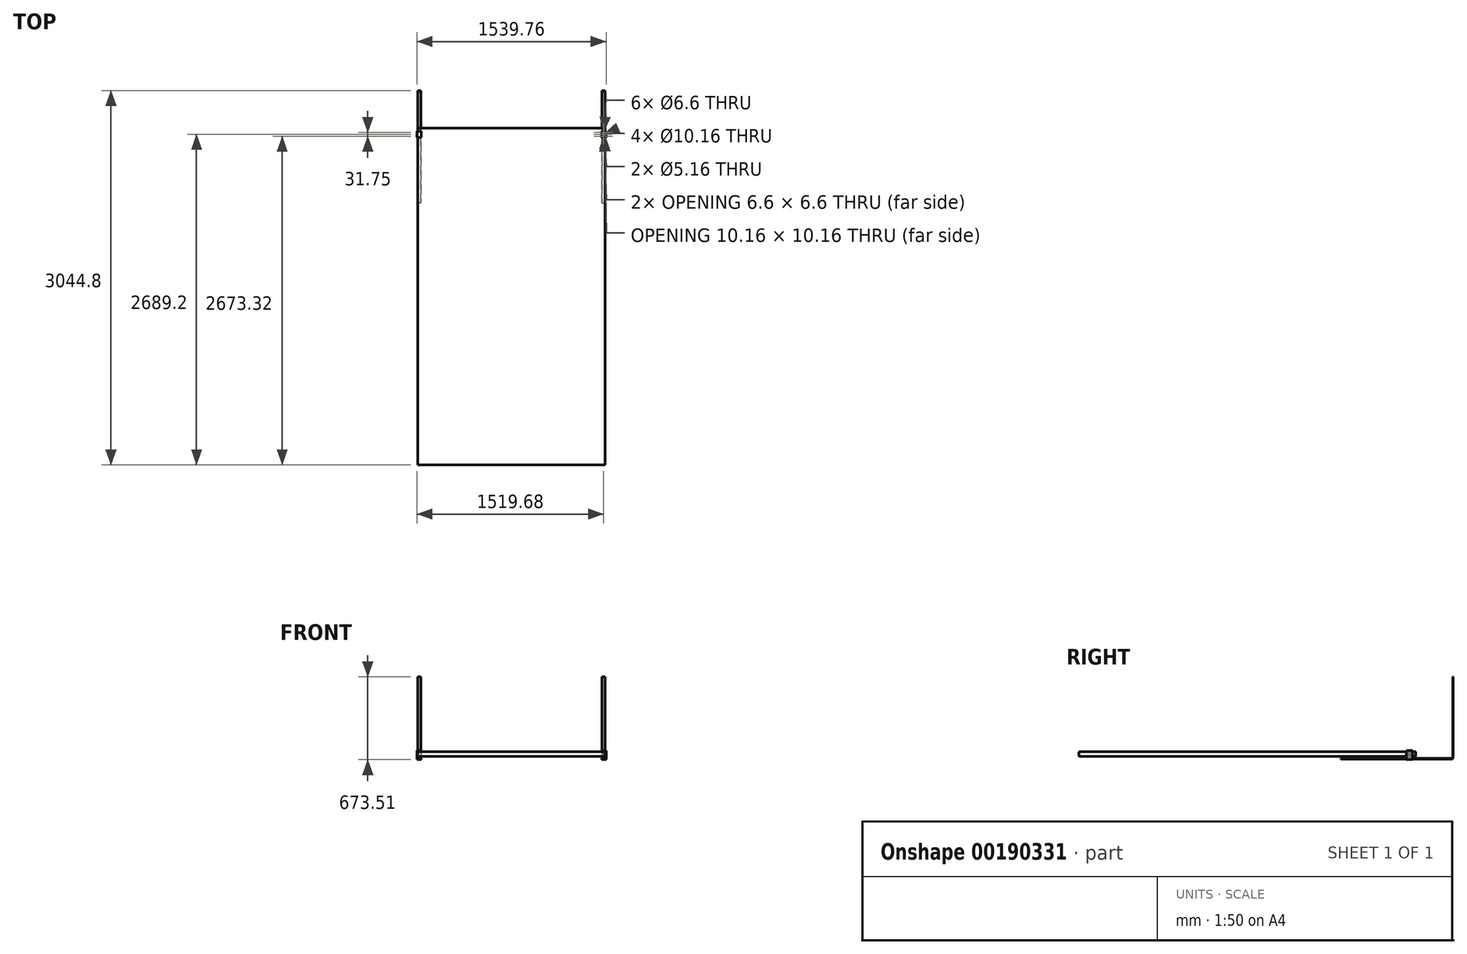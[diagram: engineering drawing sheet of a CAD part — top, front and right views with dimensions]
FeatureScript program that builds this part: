
annotation { "Feature Type Name" : "Feature", "Feature Type Description" : "" }
export const myFeature = defineFeature(function(context is Context, id is Id, definition is map)
    precondition{}
    {
        {
            var Q0;
            Q0=qCreatedBy(makeId("Top.planeOp"),FACE);
            var sketch = newSketch(context, id + "F0", { "sketchPlane" : qUnion([Q0])});
            skLineSegment(sketch, "E0.bottom", {"start": v(762.5, 1370) * mm, "end": v(-762.5, 1370) * mm});
            skLineSegment(sketch, "E0.top", {"start": v(762.5, -1370) * mm, "end": v(-762.5, -1370) * mm});
            skLineSegment(sketch, "E0.left", {"start": v(762.5, 1370) * mm, "end": v(762.5, -1370) * mm});
            skLineSegment(sketch, "E0.right", {"start": v(-762.5, 1370) * mm, "end": v(-762.5, -1370) * mm});
            skPoint(sketch, "E0.middle", {"position": v(0, 0) * mm});
            skSolve(sketch);
        }
        {
            var Q0;
            Q0 = qSketchRegion(id + "F0", true);
            extrude(context, id + "F1", {"entities" : qUnion([Q0]), "oppositeDirection" : true, "depth" : 38.1 * mm});
        }
        {
            var Q0;
            Q0=makeQuery(id+"F1.opExtrude","SWEPT_FACE",FACE,{"disambiguationData":[OSD([sQuery(id+"F0.wireOp",EDGE,"E0.bottom")])]});
            cPlane(context, id + "F2", {"entities" : qUnion([Q0]), "cplaneType" : CPlaneType.OFFSET, "offset" : 304.8 * mm, "width" : 152.4 * mm, "height" : 152.4 * mm});
        }
        {
            var Q0;
            Q0=makeQuery(id+"F1.opExtrude","SWEPT_FACE",FACE,{"disambiguationData":[OSD([sQuery(id+"F0.wireOp",EDGE,"E0.left")])]});
            cPlane(context, id + "F3", {"entities" : qUnion([Q0]), "cplaneType" : CPlaneType.OFFSET, "offset" : 0 * mm, "width" : 152.4 * mm, "height" : 152.4 * mm});
        }
        {
            var Q0;
            Q0=qCreatedBy(id+"F3.planeOp",FACE);
            var sketch = newSketch(context, id + "F4", { "sketchPlane" : qUnion([Q0])});
            skLineSegment(sketch, "E1", {"start": v(760.4, -54.06) * mm, "end": v(760.4, -58.83) * mm});
            skLineSegment(sketch, "E2", {"start": v(760.4, -58.83) * mm, "end": v(1663.69, -58.83) * mm});
            skLineSegment(sketch, "E3", {"start": v(1674.8, -47.71) * mm, "end": v(1674.8, 609.6) * mm});
            skLineSegment(sketch, "E4", {"start": v(1670.04, 609.6) * mm, "end": v(1674.8, 609.6) * mm});
            skLineSegment(sketch, "E5", {"start": v(1670.04, 609.6) * mm, "end": v(1670.04, -47.71) * mm});
            skLineSegment(sketch, "E6", {"start": v(1663.69, -54.06) * mm, "end": v(760.4, -54.06) * mm});
            skPoint(sketch, "E7.visualSharp", {"position": v(1670.04, -54.06) * mm});
            skArc(sketch, "E7.filletArc", {"start": v(1663.69, -54.06) * mm, "mid": v(1668.18, -52.2) * mm, "end": v(1670.04, -47.71) * mm});
            skPoint(sketch, "E8.visualSharp", {"position": v(1674.8, -58.83) * mm});
            skArc(sketch, "E8.filletArc", {"start": v(1663.69, -58.83) * mm, "mid": v(1671.55, -55.57) * mm, "end": v(1674.8, -47.71) * mm});
            skSolve(sketch);
        }
        {
            var Q0;
            Q0 = qSketchRegion(id + "F4", true);
            extrude(context, id + "F5", {"entities" : qUnion([Q0]), "oppositeDirection" : true, "depth" : 25.4 * mm});
        }
        {
            var Q0;
            Q0=makeQuery(id+"F5.opExtrude","SWEPT_BODY",BODY,{"disambiguationData":[OSD([sQuery(id+"F4.wireOp",EDGE,"E1"),sQuery(id+"F4.wireOp",EDGE,"E2"),sQuery(id+"F4.wireOp",EDGE,"E3"),sQuery(id+"F4.wireOp",EDGE,"E4"),sQuery(id+"F4.wireOp",EDGE,"E5"),sQuery(id+"F4.wireOp",EDGE,"E6"),sQuery(id+"F4.wireOp",EDGE,"E7.filletArc"),sQuery(id+"F4.wireOp",EDGE,"E8.filletArc")])]});
            var Q1;
            Q1=qCreatedBy(makeId("Right.planeOp"),FACE);
            mirror(context, id + "F6", {"entities" : qUnion([Q0]), "mirrorPlane" : qUnion([Q1])});
        }
        {
            var Q0;
            Q0=makeQuery(id+"F1.opExtrude","SWEPT_FACE",FACE,{"disambiguationData":[OSD([sQuery(id+"F0.wireOp",EDGE,"E0.bottom")])]});
            cPlane(context, id + "F7", {"entities" : qUnion([Q0]), "cplaneType" : CPlaneType.OFFSET, "offset" : 25.4 * mm, "oppositeDirection" : true, "width" : 152.4 * mm, "height" : 152.4 * mm});
        }
        {
            var Q0;
            Q0=qCreatedBy(id+"F7.planeOp",FACE);
            var sketch = newSketch(context, id + "F8", { "sketchPlane" : qUnion([Q0])});
            skLineSegment(sketch, "E9", {"start": v(-732.9, 5.08) * mm, "end": v(-766.7, 5.08) * mm});
            skLineSegment(sketch, "E10", {"start": v(-766.7, 5.08) * mm, "end": v(-766.7, -58.83) * mm});
            skLineSegment(sketch, "E11", {"start": v(-766.7, -58.83) * mm, "end": v(-732.9, -58.83) * mm});
            skLineSegment(sketch, "E12", {"start": v(-732.9, -58.83) * mm, "end": v(-732.9, -63.9) * mm});
            skLineSegment(sketch, "E13", {"start": v(-732.9, -63.9) * mm, "end": v(-769.88, -63.9) * mm});
            skLineSegment(sketch, "E14", {"start": v(-769.88, -63.9) * mm, "end": v(-769.88, 10.16) * mm});
            skLineSegment(sketch, "E15", {"start": v(-769.88, 10.16) * mm, "end": v(-732.9, 10.16) * mm});
            skLineSegment(sketch, "E16", {"start": v(-732.9, 10.16) * mm, "end": v(-732.9, 5.08) * mm});
            skLineSegment(sketch, "E17", {"start": v(0, 0) * mm, "end": v(0, 391.25) * mm, "construction": true});
            skLineSegment(sketch, "E18.MirrorCS", {"start": v(732.9, -58.83) * mm, "end": v(732.9, -63.9) * mm});
            skLineSegment(sketch, "E19.MirrorCS", {"start": v(732.9, 10.16) * mm, "end": v(732.9, 5.08) * mm});
            skLineSegment(sketch, "E20.MirrorCS", {"start": v(766.7, -58.83) * mm, "end": v(732.9, -58.83) * mm});
            skLineSegment(sketch, "E21.MirrorCS", {"start": v(766.7, 5.08) * mm, "end": v(766.7, -58.83) * mm});
            skLineSegment(sketch, "E22.MirrorCS", {"start": v(732.9, 5.08) * mm, "end": v(766.7, 5.08) * mm});
            skLineSegment(sketch, "E23.MirrorCS", {"start": v(769.88, 10.16) * mm, "end": v(732.9, 10.16) * mm});
            skLineSegment(sketch, "E24.MirrorCS", {"start": v(732.9, -63.9) * mm, "end": v(769.88, -63.9) * mm});
            skLineSegment(sketch, "E25.MirrorCS", {"start": v(769.88, -63.9) * mm, "end": v(769.88, 10.16) * mm});
            skLineSegment(sketch, "E26", {"start": v(-749.8, -58.83) * mm, "end": v(-749.8, 51.3) * mm, "construction": true});
            skSolve(sketch);
        }
        {
            var Q0;
            Q0 = qSketchRegion(id + "F8", true);
            extrude(context, id + "F9", {"entities" : qUnion([Q0]), "oppositeDirection" : true, "depth" : 50.8 * mm});
        }
        {
            var Q0;
            Q0=makeQuery(id+"F5.opExtrude","SWEPT_FACE",FACE,{"disambiguationData":[OSD([sQuery(id+"F4.wireOp",EDGE,"E6")])]});
            var sketch = newSketch(context, id + "F10", { "sketchPlane" : qUnion([Q0])});
            skLineSegment(sketch, "E27", {"start": v(766.7, 1319.2) * mm, "end": v(732.9, 1319.2) * mm, "construction": true});
            skLineSegment(sketch, "E28", {"start": v(749.8, 1344.6) * mm, "end": v(749.8, 1293.8) * mm, "construction": true});
            skCircle(sketch, "E29", {"center": v(749.8, 1335.08) * mm, "radius": 2.58 * mm});
            skCircle(sketch, "E30", {"center": v(749.8, 1303.33) * mm, "radius": 2.58 * mm});
            skCircle(sketch, "E31", {"center": v(749.8, 1319.2) * mm, "radius": 5.08 * mm});
            skSolve(sketch);
        }
        {
            var Q0;
            Q0 = qSketchRegion(id + "F10", true);
            extrude(context, id + "F11", {"entities" : qUnion([Q0]), "operationType" : NewBodyOperationType.REMOVE, "endBound" : BoundingType.THROUGH_ALL, "oppositeDirection" : true, "depth" : 25.4 * mm});
        }
        {
            var Q0;
            Q0=makeQuery(id+"F5.opExtrude","SWEPT_FACE",FACE,{"disambiguationData":[OSD([sQuery(id+"F4.wireOp",EDGE,"E2")])]});
            var sketch = newSketch(context, id + "F12", { "sketchPlane" : qUnion([Q0])});
            skCircle(sketch, "E32", {"center": v(749.8, -1335.08) * mm, "radius": 3.3 * mm});
            skCircle(sketch, "E33", {"center": v(749.8, -1303.33) * mm, "radius": 3.3 * mm});
            skCircle(sketch, "E34", {"center": v(749.8, -1319.2) * mm, "radius": 5.08 * mm});
            skSolve(sketch);
        }
        {
            var Q0;
            Q0 = qSketchRegion(id + "F12", true);
            extrude(context, id + "F13", {"entities" : qUnion([Q0]), "operationType" : NewBodyOperationType.REMOVE, "endBound" : BoundingType.THROUGH_ALL, "oppositeDirection" : true, "depth" : 25.4 * mm});
        }
    });
